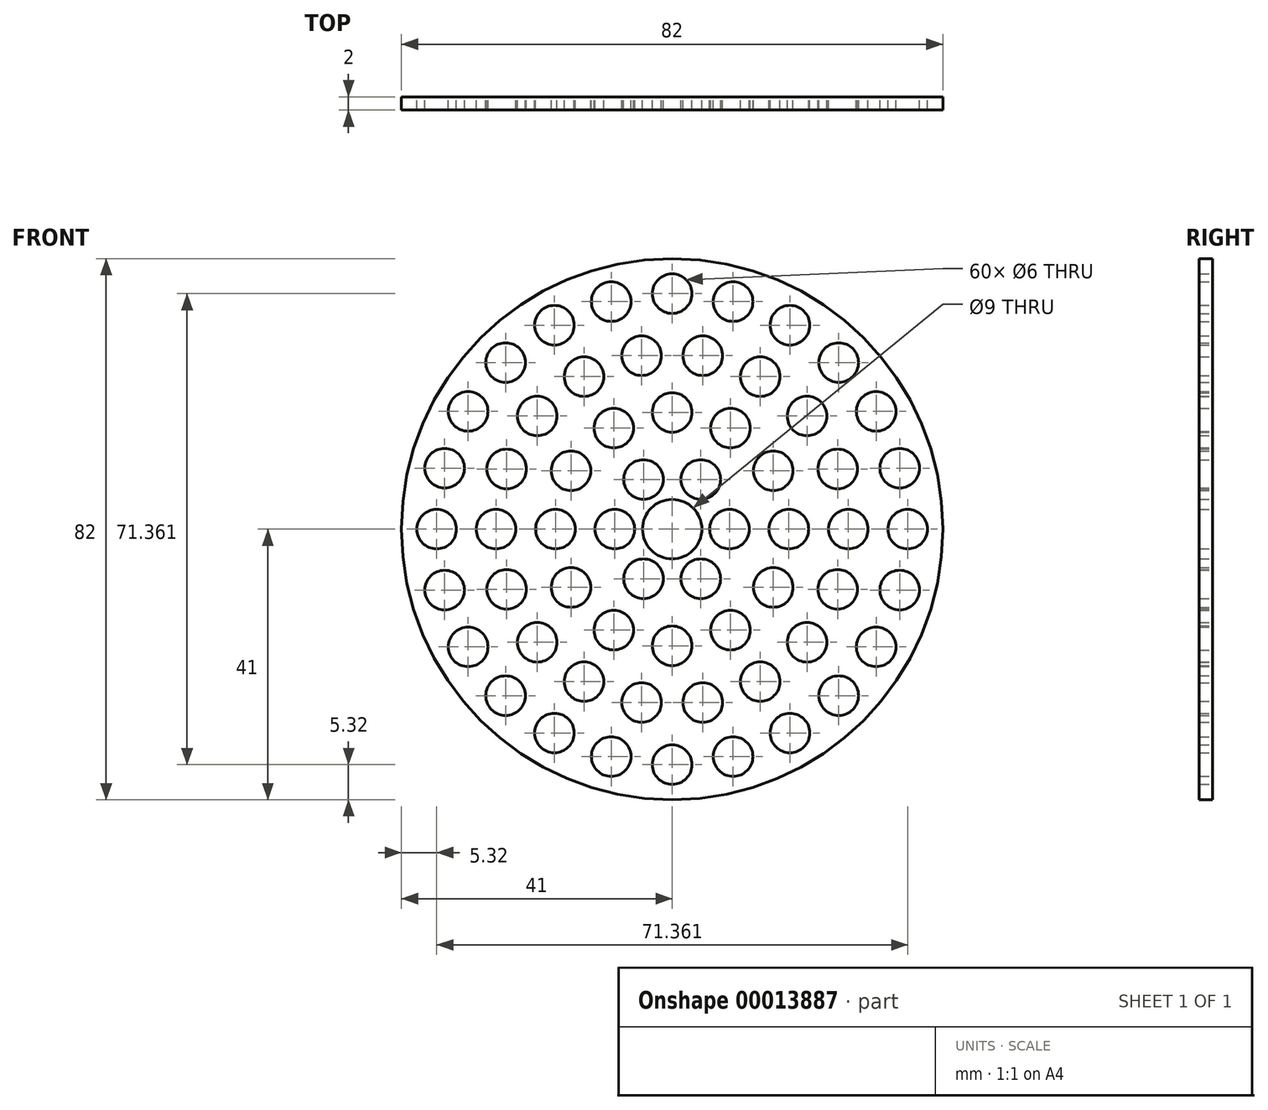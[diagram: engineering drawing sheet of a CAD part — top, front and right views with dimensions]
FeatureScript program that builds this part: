
annotation { "Feature Type Name" : "Feature", "Feature Type Description" : "" }
export const myFeature = defineFeature(function(context is Context, id is Id, definition is map)
    precondition{}
    {
        {
            var Q0;
            Q0=qCreatedBy(makeId("Front.planeOp"),FACE);
            var sketch = newSketch(context, id + "F0", { "sketchPlane" : qUnion([Q0])});
            skCircle(sketch, "E0", {"center": v(0, 0) * mm, "radius": 41 * mm});
            skSolve(sketch);
        }
        {
            var Q0;
            Q0=makeQuery(id+"F0.imprint","IMPRINT",FACE,{"disambiguationData":[TD([[makeQuery(id+"F0.imprint","IMPRINT",EDGE,{"derivedFrom":sQuery(id+"F0.wireOp",EDGE,"E0")}),1.0]])]});
            var sketch = newSketch(context, id + "F1", { "sketchPlane" : qUnion([Q0])});
            skCircle(sketch, "E1", {"center": v(0, 35.68) * mm, "radius": 3 * mm});
            skCircle(sketch, "E2.1.0", {"center": v(9.23, 34.46) * mm, "radius": 3 * mm});
            skCircle(sketch, "E2.2.0", {"center": v(17.84, 30.9) * mm, "radius": 3 * mm});
            skCircle(sketch, "E2.3.0", {"center": v(25.23, 25.23) * mm, "radius": 3 * mm});
            skCircle(sketch, "E2.4.0", {"center": v(30.9, 17.84) * mm, "radius": 3 * mm});
            skCircle(sketch, "E2.5.0", {"center": v(34.46, 9.23) * mm, "radius": 3 * mm});
            skCircle(sketch, "E2.6.0", {"center": v(35.68, 0) * mm, "radius": 3 * mm});
            skCircle(sketch, "E2.7.0", {"center": v(34.46, -9.23) * mm, "radius": 3 * mm});
            skCircle(sketch, "E2.8.0", {"center": v(30.9, -17.84) * mm, "radius": 3 * mm});
            skCircle(sketch, "E2.9.0", {"center": v(25.23, -25.23) * mm, "radius": 3 * mm});
            skCircle(sketch, "E2.10.0", {"center": v(17.84, -30.9) * mm, "radius": 3 * mm});
            skCircle(sketch, "E2.11.0", {"center": v(9.23, -34.46) * mm, "radius": 3 * mm});
            skCircle(sketch, "E2.12.0", {"center": v(0, -35.68) * mm, "radius": 3 * mm});
            skCircle(sketch, "E2.13.0", {"center": v(-9.23, -34.46) * mm, "radius": 3 * mm});
            skCircle(sketch, "E2.14.0", {"center": v(-17.84, -30.9) * mm, "radius": 3 * mm});
            skCircle(sketch, "E2.15.0", {"center": v(-25.23, -25.23) * mm, "radius": 3 * mm});
            skCircle(sketch, "E2.16.0", {"center": v(-30.9, -17.84) * mm, "radius": 3 * mm});
            skCircle(sketch, "E2.17.0", {"center": v(-34.46, -9.23) * mm, "radius": 3 * mm});
            skCircle(sketch, "E2.18.0", {"center": v(-35.68, 0) * mm, "radius": 3 * mm});
            skCircle(sketch, "E2.19.0", {"center": v(-34.46, 9.23) * mm, "radius": 3 * mm});
            skCircle(sketch, "E2.20.0", {"center": v(-30.9, 17.84) * mm, "radius": 3 * mm});
            skCircle(sketch, "E2.21.0", {"center": v(-25.23, 25.23) * mm, "radius": 3 * mm});
            skCircle(sketch, "E2.22.0", {"center": v(-17.84, 30.9) * mm, "radius": 3 * mm});
            skCircle(sketch, "E2.23.0", {"center": v(-9.23, 34.46) * mm, "radius": 3 * mm});
            skPoint(sketch, "E2.center", {"position": v(0, 0) * mm});
            skLineSegment(sketch, "E2.anchor1", {"start": v(0, 0) * mm, "end": v(0, 35.68) * mm, "construction": true});
            skLineSegment(sketch, "E2.anchor2", {"start": v(0, 0) * mm, "end": v(-9.23, 34.46) * mm, "construction": true});
            skCircle(sketch, "E3.1.0.0", {"center": v(-26.68, 0) * mm, "radius": 3 * mm});
            skCircle(sketch, "E3.2.0.0", {"center": v(-17.68, 0) * mm, "radius": 3 * mm});
            skCircle(sketch, "E3.3.0.0", {"center": v(-8.68, 0) * mm, "radius": 3 * mm});
            skLineSegment(sketch, "E3.direction1", {"start": v(-35.68, 0) * mm, "end": v(-26.68, 0) * mm, "construction": true});
            skCircle(sketch, "E4.1.0", {"center": v(-25.07, -9.13) * mm, "radius": 3 * mm});
            skCircle(sketch, "E4.2.0", {"center": v(-20.44, -17.15) * mm, "radius": 3 * mm});
            skCircle(sketch, "E4.3.0", {"center": v(-13.34, -23.1) * mm, "radius": 3 * mm});
            skCircle(sketch, "E4.4.0", {"center": v(-4.63, -26.27) * mm, "radius": 3 * mm});
            skCircle(sketch, "E4.5.0", {"center": v(4.63, -26.27) * mm, "radius": 3 * mm});
            skCircle(sketch, "E4.6.0", {"center": v(13.34, -23.1) * mm, "radius": 3 * mm});
            skCircle(sketch, "E4.7.0", {"center": v(20.44, -17.15) * mm, "radius": 3 * mm});
            skCircle(sketch, "E4.8.0", {"center": v(25.07, -9.13) * mm, "radius": 3 * mm});
            skCircle(sketch, "E4.9.0", {"center": v(26.68, 0) * mm, "radius": 3 * mm});
            skCircle(sketch, "E4.10.0", {"center": v(25.07, 9.13) * mm, "radius": 3 * mm});
            skCircle(sketch, "E4.11.0", {"center": v(20.44, 17.15) * mm, "radius": 3 * mm});
            skCircle(sketch, "E4.12.0", {"center": v(13.34, 23.1) * mm, "radius": 3 * mm});
            skCircle(sketch, "E4.13.0", {"center": v(4.63, 26.27) * mm, "radius": 3 * mm});
            skCircle(sketch, "E4.14.0", {"center": v(-4.63, 26.27) * mm, "radius": 3 * mm});
            skCircle(sketch, "E4.15.0", {"center": v(-13.34, 23.1) * mm, "radius": 3 * mm});
            skCircle(sketch, "E4.16.0", {"center": v(-20.44, 17.15) * mm, "radius": 3 * mm});
            skCircle(sketch, "E4.17.0", {"center": v(-25.07, 9.13) * mm, "radius": 3 * mm});
            skCircle(sketch, "E5.1.0", {"center": v(-15.31, 8.84) * mm, "radius": 3 * mm});
            skCircle(sketch, "E5.2.0", {"center": v(-8.84, 15.31) * mm, "radius": 3 * mm});
            skCircle(sketch, "E5.3.0", {"center": v(0, 17.68) * mm, "radius": 3 * mm});
            skCircle(sketch, "E5.4.0", {"center": v(8.84, 15.31) * mm, "radius": 3 * mm});
            skCircle(sketch, "E5.5.0", {"center": v(15.31, 8.84) * mm, "radius": 3 * mm});
            skCircle(sketch, "E5.6.0", {"center": v(17.68, 0) * mm, "radius": 3 * mm});
            skCircle(sketch, "E5.7.0", {"center": v(15.31, -8.84) * mm, "radius": 3 * mm});
            skCircle(sketch, "E5.8.0", {"center": v(8.84, -15.31) * mm, "radius": 3 * mm});
            skLineSegment(sketch, "E5.anchor1", {"start": v(0, 0) * mm, "end": v(-17.68, 0) * mm, "construction": true});
            skLineSegment(sketch, "E5.anchor2", {"start": v(0, 0) * mm, "end": v(-15.31, -8.84) * mm, "construction": true});
            skCircle(sketch, "E6.1.9.0", {"center": v(0, -17.68) * mm, "radius": 3 * mm});
            skCircle(sketch, "E6.1.10.0", {"center": v(-8.84, -15.31) * mm, "radius": 3 * mm});
            skCircle(sketch, "E6.1.11.0", {"center": v(-15.31, -8.84) * mm, "radius": 3 * mm});
            skCircle(sketch, "E7.1.0", {"center": v(-4.34, -7.52) * mm, "radius": 3 * mm});
            skCircle(sketch, "E7.2.0", {"center": v(4.34, -7.52) * mm, "radius": 3 * mm});
            skCircle(sketch, "E7.3.0", {"center": v(8.68, 0) * mm, "radius": 3 * mm});
            skCircle(sketch, "E7.4.0", {"center": v(4.34, 7.52) * mm, "radius": 3 * mm});
            skCircle(sketch, "E7.5.0", {"center": v(-4.34, 7.52) * mm, "radius": 3 * mm});
            skSolve(sketch);
        }
        {
            var Q0;
            Q0=makeQuery(id+"F1.imprint","IMPRINT",FACE,{"disambiguationData":[TD([[makeQuery(id+"F1.imprint","IMPRINT",EDGE,{"derivedFrom":sQuery(id+"F1.wireOp",EDGE,"E1")}),-1.0]])]});
            extrude(context, id + "F2", {"entities" : qUnion([Q0]), "depth" : 2 * mm});
        }
        {
            var Q0;
            Q0=sQuery(id+"F0.wireOp",VERTEX,"E0.center");
            var Q1;
            Q1=makeQuery(id+"F2.opExtrude","SWEPT_BODY",BODY,{"disambiguationData":[OSD([sQuery(id+"F0.wireOp",EDGE,"E0"),sQuery(id+"F1.wireOp",EDGE,"E1"),sQuery(id+"F1.wireOp",EDGE,"E2.1.0"),sQuery(id+"F1.wireOp",EDGE,"E2.2.0"),sQuery(id+"F1.wireOp",EDGE,"E2.3.0"),sQuery(id+"F1.wireOp",EDGE,"E2.4.0"),sQuery(id+"F1.wireOp",EDGE,"E2.5.0"),sQuery(id+"F1.wireOp",EDGE,"E2.6.0"),sQuery(id+"F1.wireOp",EDGE,"E2.7.0"),sQuery(id+"F1.wireOp",EDGE,"E2.8.0"),sQuery(id+"F1.wireOp",EDGE,"E2.9.0"),sQuery(id+"F1.wireOp",EDGE,"E2.10.0"),sQuery(id+"F1.wireOp",EDGE,"E2.11.0"),sQuery(id+"F1.wireOp",EDGE,"E2.12.0"),sQuery(id+"F1.wireOp",EDGE,"E2.13.0"),sQuery(id+"F1.wireOp",EDGE,"E2.14.0"),sQuery(id+"F1.wireOp",EDGE,"E2.15.0"),sQuery(id+"F1.wireOp",EDGE,"E2.16.0"),sQuery(id+"F1.wireOp",EDGE,"E2.17.0"),sQuery(id+"F1.wireOp",EDGE,"E2.18.0"),sQuery(id+"F1.wireOp",EDGE,"E2.19.0"),sQuery(id+"F1.wireOp",EDGE,"E2.20.0"),sQuery(id+"F1.wireOp",EDGE,"E2.21.0"),sQuery(id+"F1.wireOp",EDGE,"E2.22.0"),sQuery(id+"F1.wireOp",EDGE,"E2.23.0"),sQuery(id+"F1.wireOp",EDGE,"E3.1.0.0"),sQuery(id+"F1.wireOp",EDGE,"E3.2.0.0"),sQuery(id+"F1.wireOp",EDGE,"E3.3.0.0"),sQuery(id+"F1.wireOp",EDGE,"E4.1.0"),sQuery(id+"F1.wireOp",EDGE,"E4.2.0"),sQuery(id+"F1.wireOp",EDGE,"E4.3.0"),sQuery(id+"F1.wireOp",EDGE,"E4.4.0"),sQuery(id+"F1.wireOp",EDGE,"E4.5.0"),sQuery(id+"F1.wireOp",EDGE,"E4.6.0"),sQuery(id+"F1.wireOp",EDGE,"E4.7.0"),sQuery(id+"F1.wireOp",EDGE,"E4.8.0"),sQuery(id+"F1.wireOp",EDGE,"E4.9.0"),sQuery(id+"F1.wireOp",EDGE,"E4.10.0"),sQuery(id+"F1.wireOp",EDGE,"E4.11.0"),sQuery(id+"F1.wireOp",EDGE,"E4.12.0"),sQuery(id+"F1.wireOp",EDGE,"E4.13.0"),sQuery(id+"F1.wireOp",EDGE,"E4.14.0"),sQuery(id+"F1.wireOp",EDGE,"E4.15.0"),sQuery(id+"F1.wireOp",EDGE,"E4.16.0"),sQuery(id+"F1.wireOp",EDGE,"E4.17.0"),sQuery(id+"F1.wireOp",EDGE,"E5.1.0"),sQuery(id+"F1.wireOp",EDGE,"E5.2.0"),sQuery(id+"F1.wireOp",EDGE,"E5.3.0"),sQuery(id+"F1.wireOp",EDGE,"E5.4.0"),sQuery(id+"F1.wireOp",EDGE,"E5.5.0"),sQuery(id+"F1.wireOp",EDGE,"E5.6.0"),sQuery(id+"F1.wireOp",EDGE,"E5.7.0"),sQuery(id+"F1.wireOp",EDGE,"E5.8.0"),sQuery(id+"F1.wireOp",EDGE,"E6.1.9.0"),sQuery(id+"F1.wireOp",EDGE,"E6.1.10.0"),sQuery(id+"F1.wireOp",EDGE,"E6.1.11.0"),sQuery(id+"F1.wireOp",EDGE,"E7.1.0"),sQuery(id+"F1.wireOp",EDGE,"E7.2.0"),sQuery(id+"F1.wireOp",EDGE,"E7.3.0"),sQuery(id+"F1.wireOp",EDGE,"E7.4.0"),sQuery(id+"F1.wireOp",EDGE,"E7.5.0")])]});
            hole(context, id + "F3", {"style" : HoleStyle.SIMPLE, "holeDiameter" : 9 * mm, "endStyle" : HoleEndStyle.THROUGH, "oppositeDirection" : true, "locations" : qUnion([Q0]), "scope" : qUnion([Q1])});
        }
    });
